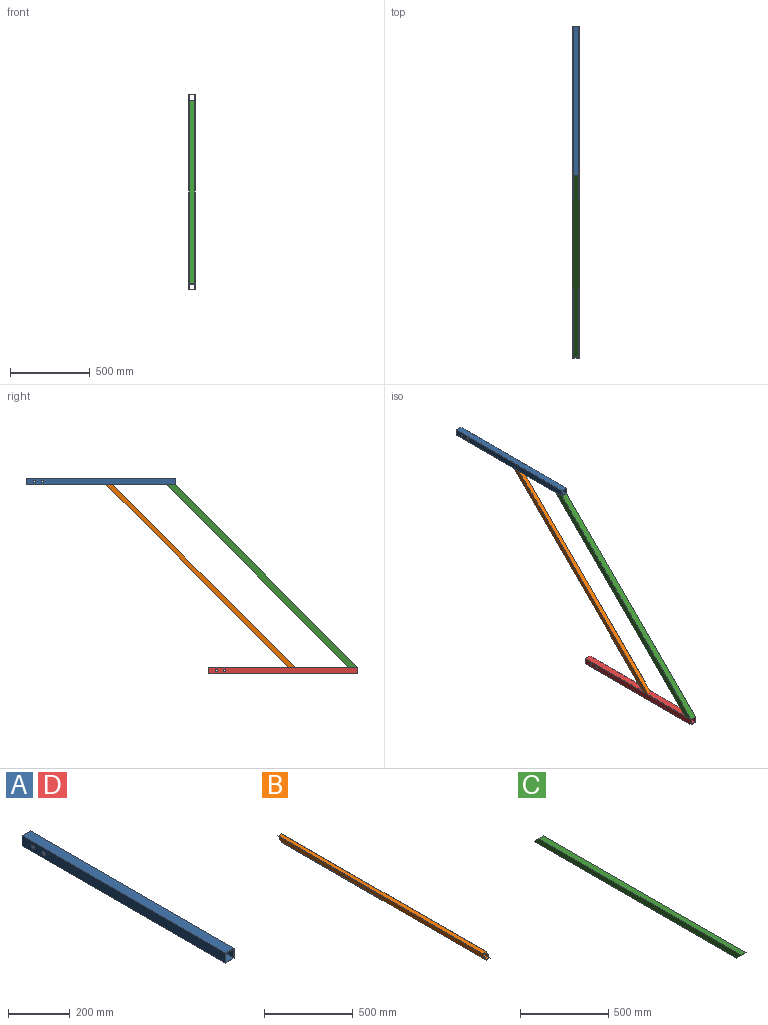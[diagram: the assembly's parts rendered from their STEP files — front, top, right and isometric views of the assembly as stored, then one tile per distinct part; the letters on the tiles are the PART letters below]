
ASSEMBLY  parts=4 mates=3
PART A: 14 faces, bbox 40x935x40 mm
  f0: plane 935x40mm, normal (0,0,1), area 37400mm2, adj f1,f7,f8,f9
  f1: plane 935x40mm, normal (-1,0,0), area 37092.1mm2, adj f0,f2,f8,f9,f12,f13
  f2: plane 935x40mm, normal (0,0,-1), area 37400mm2, adj f1,f7,f8,f9
  f3: plane 935x34mm, normal (1,0,0), area 31482.1mm2, adj f4,f6,f8,f9,f12,f13
  f4: plane 935x34mm, normal (0,0,-1), area 31790mm2, adj f3,f5,f8,f9
  f5: plane 935x34mm, normal (-1,0,0), area 31482.1mm2, adj f4,f6,f8,f9,f10,f11
  f6: plane 935x34mm, normal (0,0,1), area 31790mm2, adj f3,f5,f8,f9
  f7: plane 935x40mm, normal (1,0,0), area 37092.1mm2, adj f0,f2,f8,f9,f10,f11
  f8: plane 40x40mm, normal (0,-1,0), area 444mm2, adj f0,f1,f2,f3,f4,f5,f6,f7
  f9: plane 40x40mm, normal (0,1,0), area 444mm2, adj f0,f1,f2,f3,f4,f5,f6,f7
  f10: cylinder r=7mm len=14mm, axis (-1,0,0), area 131.9mm2, adj f5,f7
  f11: cylinder r=7mm len=14mm, axis (-1,0,0), area 131.9mm2, adj f5,f7
  f12: cylinder r=7mm len=14mm, axis (-1,0,0), area 131.9mm2, adj f1,f3
  f13: cylinder r=7mm len=14mm, axis (-1,0,0), area 131.9mm2, adj f1,f3
PART B: 10 faces, bbox 30x1657.8x30 mm
  f0: plane 1627.77x24mm, normal (0,0,1), area 39066.4mm2, adj f1,f3,f4,f5
  f1: plane 1651.77x24mm, normal (-1,0,0), area 39066.4mm2, adj f0,f2,f4,f5
  f2: plane 1627.77x24mm, normal (0,0,-1), area 39066.4mm2, adj f1,f3,f4,f5
  f3: plane 1651.77x24mm, normal (1,0,0), area 39066.4mm2, adj f0,f2,f4,f5
  f4: plane 30x30mm, normal (0,-0.71,0.71), area 458.2mm2, adj f0,f1,f2,f3,f6,f7,f8,f9
  f5: plane 30x30mm, normal (0,0.71,-0.71), area 458.2mm2, adj f0,f1,f2,f3,f6,f7,f8,f9
  f6: plane 1627.77x30mm, normal (0,0,1), area 48833mm2, adj f4,f5,f7,f9
  f7: plane 1657.77x30mm, normal (-1,0,0), area 48833mm2, adj f4,f5,f6,f8
  f8: plane 1627.77x30mm, normal (0,0,-1), area 48833mm2, adj f4,f5,f7,f9
  f9: plane 1657.77x30mm, normal (1,0,0), area 48833mm2, adj f4,f5,f6,f8
PART C: 10 faces, bbox 40x1657.8x40 mm
  f0: plane 1657.77x40mm, normal (1,0,0), area 64710.7mm2, adj f1,f7,f8,f9
  f1: plane 1617.77x40mm, normal (0,0,-1), area 64710.7mm2, adj f0,f5,f8,f9
  f2: plane 1651.77x34mm, normal (1,0,0), area 55004.1mm2, adj f3,f6,f8,f9
  f3: plane 1617.77x34mm, normal (0,0,-1), area 55004.1mm2, adj f2,f4,f8,f9
  f4: plane 1651.77x34mm, normal (-1,0,0), area 55004.1mm2, adj f3,f6,f8,f9
  f5: plane 1657.77x40mm, normal (-1,0,0), area 64710.7mm2, adj f1,f7,f8,f9
  f6: plane 1617.77x34mm, normal (0,0,1), area 55004.1mm2, adj f2,f4,f8,f9
  f7: plane 1617.77x40mm, normal (0,0,1), area 64710.7mm2, adj f0,f5,f8,f9
  f8: plane 40x40mm, normal (0,-0.71,-0.71), area 627.9mm2, adj f0,f1,f2,f3,f4,f5,f6,f7
  f9: plane 40x40mm, normal (0,0.71,0.71), area 627.9mm2, adj f0,f1,f2,f3,f4,f5,f6,f7
PART D: same geometry as A
PLACE A t=(-716.05,906.06,-235.55)mm
PLACE B rot(axis=(0,-0.92,-0.38),180deg) t=(-736.8,397.28,502.28)mm
PLACE C rot(axis=(1,0,0),45deg) t=(-756.05,27.63,493.5)mm
PLACE D t=(-716.05,-237.88,-1419.48)mm
MATE fastened B.f5 <-> A.f2  axis (0,0,1) through (-736.05,406.06,493.5)mm
MATE fastened C.f9 <-> A.f2  axis (0,0,1) through (-736.05,-28.94,493.5)mm
MATE fastened C.f8 <-> D.f0  axis (0,0,-1) through (-736.05,-1172.88,-650.44)mm
